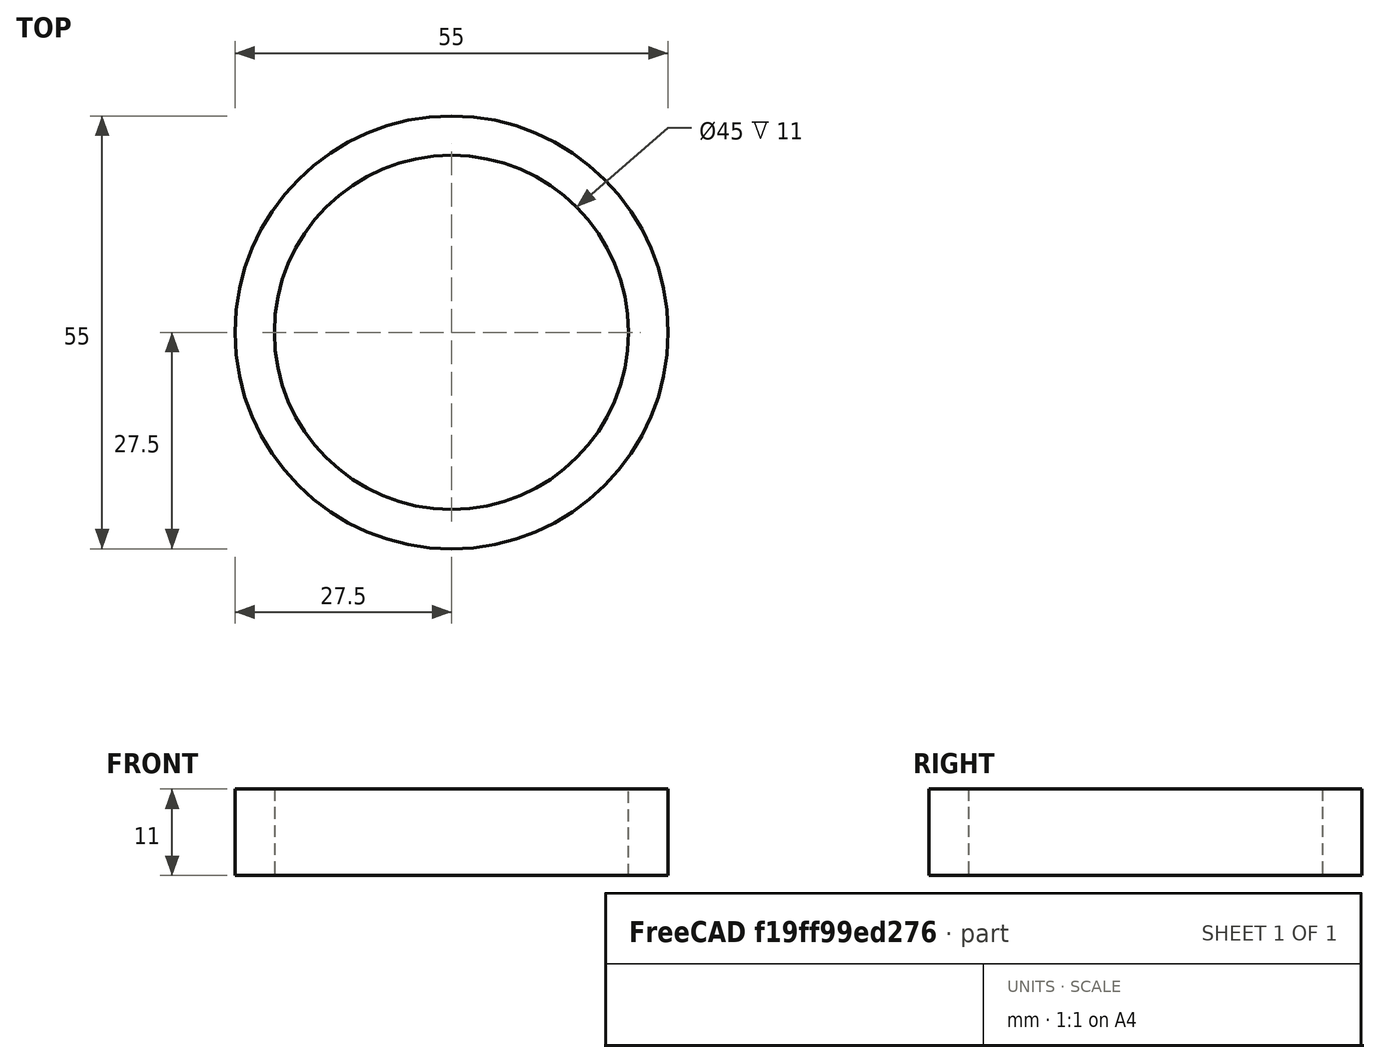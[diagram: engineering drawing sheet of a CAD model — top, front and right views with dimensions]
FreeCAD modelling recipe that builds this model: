
FCSTD DOCUMENT  (FreeCAD 0.19R24276 (Git))
Label: Ring_45x75x11_IN
License: All rights reserved
LicenseURL: http://en.wikipedia.org/wiki/All_rights_reserved
objects: Sketcher::SketchObject×1, PartDesign::Pad×1, PartDesign::Body×1
note: 4 computed .brp shape members not serialized (recipe doc carries the construction recipe); baked Part::Feature solids carry a one-line shape summary decoded from their .brp

FEATURE [Sketcher::SketchObject] Sketch
  FullyConstrained = true
  MapMode = 5
  Support = -> [XY_Plane]
  sketch-geometry (2):
    g0: Circle CenterX=0 CenterY=0 CenterZ=0 NormalX=0 NormalY=0 NormalZ=1 AngleXU=0 Radius=27.5
    g1: Circle CenterX=0 CenterY=0 CenterZ=0 NormalX=0 NormalY=0 NormalZ=1 AngleXU=0 Radius=22.5
  constraints (4):
    c: Coincident(g1,g0)
    c: Diameter(g1) = 45
    c: Diameter(g0) = 55
    c: Coincident(g0,g-1)
FEATURE [PartDesign::Pad] Pad
  Direction = (1,1,1)
  Length = 11
  Length2 = 100
  Profile = -> Sketch
  Type = 0
FEATURE [PartDesign::Body] Body  label="Body_ring_in"
  Group = -> [Sketch,Pad]
  Origin = -> Origin
  Tip = -> Pad
